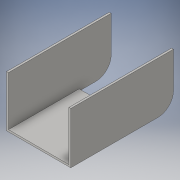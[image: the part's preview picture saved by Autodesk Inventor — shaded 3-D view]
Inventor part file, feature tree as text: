
AUTODESK INVENTOR PART (.ipt)
format: ipt  version: 2016 (Build 200138000, 138)  size: 111,616 bytes
history: native  units: in
note: dims shown in document units (in); Inventor stores cm internally (conversion verified against a paired STEP export)
features: extrude x3, sketch x3, fillet x1
ambient origin geometry x8: Origin, YZ Plane, XZ Plane, XY Plane, X Axis, Y Axis, Z Axis, Center Point
bodies: Solid1 (feature_tree)
feature tree (7):
  extrude  "Extrusion1"  Depth=8.0in
  extrude  "Extrusion2"  Depth=4.7in
  extrude  "Extrusion3"  Depth=2.5in
  fillet  "Fillet1"  Radius=0.15in
  sketch  "Sketch1"  dims[d0=5.0in d1=8.0in]
  sketch  "Sketch3"  dims[d2=4.0in d3=0.0in d4=4.7in]
  sketch  "Sketch4"  dims[d5=3.85in d6=0.0in d7=2.5in d8=0.15in d9=0.0in d10=1.2in]
